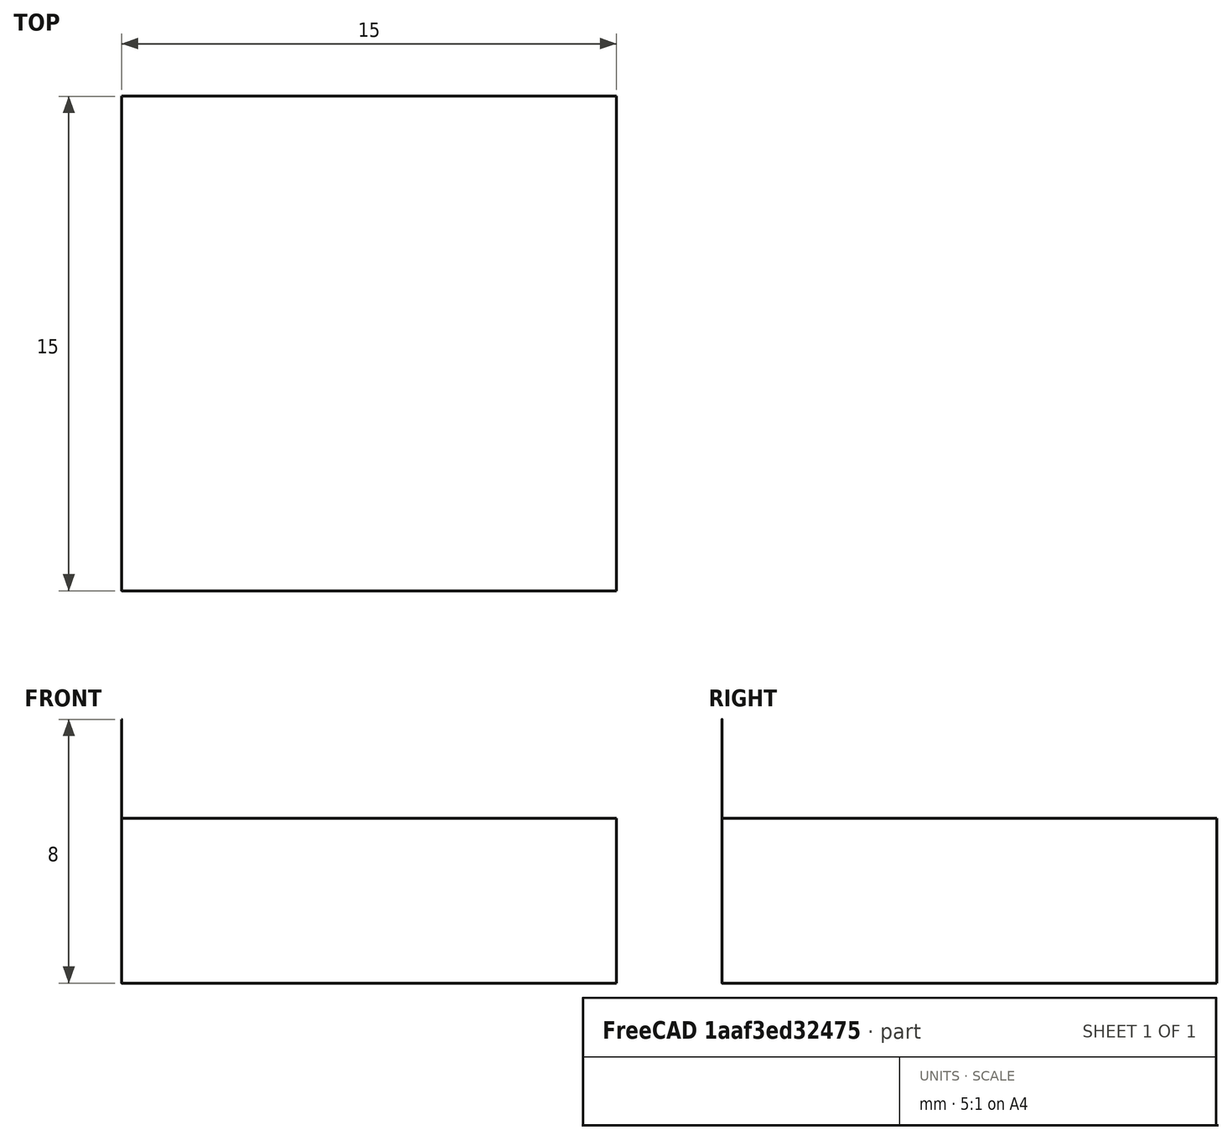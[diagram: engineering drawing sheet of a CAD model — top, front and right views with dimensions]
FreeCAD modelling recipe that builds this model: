
FCSTD DOCUMENT  (FreeCAD 1.0R39109 (Git))
Label: BoxWith36GridPockets
License: All rights reserved
LicenseURL: https://en.wikipedia.org/wiki/All_rights_reserved
objects: Part::Box×37, Part::Cut×36, Part::FeaturePython×3, App::DocumentObjectGroup×3, Path::FeaturePython×3, App::FeaturePython×1
note: 77 computed .brp shape members not serialized (recipe doc carries the construction recipe); baked Part::Feature solids carry a one-line shape summary decoded from their .brp

FEATURE [Part::Box] Box
  AttacherType = Attacher::AttachEngine3D
  Height = 5
  Length = 15
  Width = 15
FEATURE [Part::Box] Pocket_0_0
  AttacherType = Attacher::AttachEngine3D
  Height = 0.01
  Length = 0.2
  Placement = pos=(1.97143,1.97143,4.99) rot=(0,0,1;0rad)
  Width = 0.2
FEATURE [Part::Box] Pocket_0_1
  AttacherType = Attacher::AttachEngine3D
  Height = 0.01
  Length = 0.2
  Placement = pos=(4.14286,1.97143,4.99) rot=(0,0,1;0rad)
  Width = 0.2
FEATURE [Part::Box] Pocket_0_2
  AttacherType = Attacher::AttachEngine3D
  Height = 0.01
  Length = 0.2
  Placement = pos=(6.31429,1.97143,4.99) rot=(0,0,1;0rad)
  Width = 0.2
FEATURE [Part::Box] Pocket_0_3
  AttacherType = Attacher::AttachEngine3D
  Height = 0.01
  Length = 0.2
  Placement = pos=(8.48571,1.97143,4.99) rot=(0,0,1;0rad)
  Width = 0.2
FEATURE [Part::Box] Pocket_0_4
  AttacherType = Attacher::AttachEngine3D
  Height = 0.01
  Length = 0.2
  Placement = pos=(10.6571,1.97143,4.99) rot=(0,0,1;0rad)
  Width = 0.2
FEATURE [Part::Box] Pocket_0_5
  AttacherType = Attacher::AttachEngine3D
  Height = 0.01
  Length = 0.2
  Placement = pos=(12.8286,1.97143,4.99) rot=(0,0,1;0rad)
  Width = 0.2
FEATURE [Part::Box] Pocket_1_0
  AttacherType = Attacher::AttachEngine3D
  Height = 0.01
  Length = 0.2
  Placement = pos=(1.97143,4.14286,4.99) rot=(0,0,1;0rad)
  Width = 0.2
FEATURE [Part::Box] Pocket_1_1
  AttacherType = Attacher::AttachEngine3D
  Height = 0.01
  Length = 0.2
  Placement = pos=(4.14286,4.14286,4.99) rot=(0,0,1;0rad)
  Width = 0.2
FEATURE [Part::Box] Pocket_1_2
  AttacherType = Attacher::AttachEngine3D
  Height = 0.01
  Length = 0.2
  Placement = pos=(6.31429,4.14286,4.99) rot=(0,0,1;0rad)
  Width = 0.2
FEATURE [Part::Box] Pocket_1_3
  AttacherType = Attacher::AttachEngine3D
  Height = 0.01
  Length = 0.2
  Placement = pos=(8.48571,4.14286,4.99) rot=(0,0,1;0rad)
  Width = 0.2
FEATURE [Part::Box] Pocket_1_4
  AttacherType = Attacher::AttachEngine3D
  Height = 0.01
  Length = 0.2
  Placement = pos=(10.6571,4.14286,4.99) rot=(0,0,1;0rad)
  Width = 0.2
FEATURE [Part::Box] Pocket_1_5
  AttacherType = Attacher::AttachEngine3D
  Height = 0.01
  Length = 0.2
  Placement = pos=(12.8286,4.14286,4.99) rot=(0,0,1;0rad)
  Width = 0.2
FEATURE [Part::Box] Pocket_2_0
  AttacherType = Attacher::AttachEngine3D
  Height = 0.01
  Length = 0.2
  Placement = pos=(1.97143,6.31429,4.99) rot=(0,0,1;0rad)
  Width = 0.2
FEATURE [Part::Box] Pocket_2_1
  AttacherType = Attacher::AttachEngine3D
  Height = 0.01
  Length = 0.2
  Placement = pos=(4.14286,6.31429,4.99) rot=(0,0,1;0rad)
  Width = 0.2
FEATURE [Part::Box] Pocket_2_2
  AttacherType = Attacher::AttachEngine3D
  Height = 0.01
  Length = 0.2
  Placement = pos=(6.31429,6.31429,4.99) rot=(0,0,1;0rad)
  Width = 0.2
FEATURE [Part::Box] Pocket_2_3
  AttacherType = Attacher::AttachEngine3D
  Height = 0.01
  Length = 0.2
  Placement = pos=(8.48571,6.31429,4.99) rot=(0,0,1;0rad)
  Width = 0.2
FEATURE [Part::Box] Pocket_2_4
  AttacherType = Attacher::AttachEngine3D
  Height = 0.01
  Length = 0.2
  Placement = pos=(10.6571,6.31429,4.99) rot=(0,0,1;0rad)
  Width = 0.2
FEATURE [Part::Box] Pocket_2_5
  AttacherType = Attacher::AttachEngine3D
  Height = 0.01
  Length = 0.2
  Placement = pos=(12.8286,6.31429,4.99) rot=(0,0,1;0rad)
  Width = 0.2
FEATURE [Part::Box] Pocket_3_0
  AttacherType = Attacher::AttachEngine3D
  Height = 0.01
  Length = 0.2
  Placement = pos=(1.97143,8.48571,4.99) rot=(0,0,1;0rad)
  Width = 0.2
FEATURE [Part::Box] Pocket_3_1
  AttacherType = Attacher::AttachEngine3D
  Height = 0.01
  Length = 0.2
  Placement = pos=(4.14286,8.48571,4.99) rot=(0,0,1;0rad)
  Width = 0.2
FEATURE [Part::Box] Pocket_3_2
  AttacherType = Attacher::AttachEngine3D
  Height = 0.01
  Length = 0.2
  Placement = pos=(6.31429,8.48571,4.99) rot=(0,0,1;0rad)
  Width = 0.2
FEATURE [Part::Box] Pocket_3_3
  AttacherType = Attacher::AttachEngine3D
  Height = 0.01
  Length = 0.2
  Placement = pos=(8.48571,8.48571,4.99) rot=(0,0,1;0rad)
  Width = 0.2
FEATURE [Part::Box] Pocket_3_4
  AttacherType = Attacher::AttachEngine3D
  Height = 0.01
  Length = 0.2
  Placement = pos=(10.6571,8.48571,4.99) rot=(0,0,1;0rad)
  Width = 0.2
FEATURE [Part::Box] Pocket_3_5
  AttacherType = Attacher::AttachEngine3D
  Height = 0.01
  Length = 0.2
  Placement = pos=(12.8286,8.48571,4.99) rot=(0,0,1;0rad)
  Width = 0.2
FEATURE [Part::Box] Pocket_4_0
  AttacherType = Attacher::AttachEngine3D
  Height = 0.01
  Length = 0.2
  Placement = pos=(1.97143,10.6571,4.99) rot=(0,0,1;0rad)
  Width = 0.2
FEATURE [Part::Box] Pocket_4_1
  AttacherType = Attacher::AttachEngine3D
  Height = 0.01
  Length = 0.2
  Placement = pos=(4.14286,10.6571,4.99) rot=(0,0,1;0rad)
  Width = 0.2
FEATURE [Part::Box] Pocket_4_2
  AttacherType = Attacher::AttachEngine3D
  Height = 0.01
  Length = 0.2
  Placement = pos=(6.31429,10.6571,4.99) rot=(0,0,1;0rad)
  Width = 0.2
FEATURE [Part::Box] Pocket_4_3
  AttacherType = Attacher::AttachEngine3D
  Height = 0.01
  Length = 0.2
  Placement = pos=(8.48571,10.6571,4.99) rot=(0,0,1;0rad)
  Width = 0.2
FEATURE [Part::Box] Pocket_4_4
  AttacherType = Attacher::AttachEngine3D
  Height = 0.01
  Length = 0.2
  Placement = pos=(10.6571,10.6571,4.99) rot=(0,0,1;0rad)
  Width = 0.2
FEATURE [Part::Box] Pocket_4_5
  AttacherType = Attacher::AttachEngine3D
  Height = 0.01
  Length = 0.2
  Placement = pos=(12.8286,10.6571,4.99) rot=(0,0,1;0rad)
  Width = 0.2
FEATURE [Part::Box] Pocket_5_0
  AttacherType = Attacher::AttachEngine3D
  Height = 0.01
  Length = 0.2
  Placement = pos=(1.97143,12.8286,4.99) rot=(0,0,1;0rad)
  Width = 0.2
FEATURE [Part::Box] Pocket_5_1
  AttacherType = Attacher::AttachEngine3D
  Height = 0.01
  Length = 0.2
  Placement = pos=(4.14286,12.8286,4.99) rot=(0,0,1;0rad)
  Width = 0.2
FEATURE [Part::Box] Pocket_5_2
  AttacherType = Attacher::AttachEngine3D
  Height = 0.01
  Length = 0.2
  Placement = pos=(6.31429,12.8286,4.99) rot=(0,0,1;0rad)
  Width = 0.2
FEATURE [Part::Box] Pocket_5_3
  AttacherType = Attacher::AttachEngine3D
  Height = 0.01
  Length = 0.2
  Placement = pos=(8.48571,12.8286,4.99) rot=(0,0,1;0rad)
  Width = 0.2
FEATURE [Part::Box] Pocket_5_4
  AttacherType = Attacher::AttachEngine3D
  Height = 0.01
  Length = 0.2
  Placement = pos=(10.6571,12.8286,4.99) rot=(0,0,1;0rad)
  Width = 0.2
FEATURE [Part::Box] Pocket_5_5
  AttacherType = Attacher::AttachEngine3D
  Height = 0.01
  Length = 0.2
  Placement = pos=(12.8286,12.8286,4.99) rot=(0,0,1;0rad)
  Width = 0.2
FEATURE [Part::Cut] Cut  label="Cut_0"
  Base = -> Box
  Refine = true
  Tool = -> Pocket_0_0
FEATURE [Part::Cut] Cut001  label="Cut_1"
  Base = -> Cut
  Refine = true
  Tool = -> Pocket_0_1
FEATURE [Part::Cut] Cut002  label="Cut_2"
  Base = -> Cut001
  Refine = true
  Tool = -> Pocket_0_2
FEATURE [Part::Cut] Cut003  label="Cut_3"
  Base = -> Cut002
  Refine = true
  Tool = -> Pocket_0_3
FEATURE [Part::Cut] Cut004  label="Cut_4"
  Base = -> Cut003
  Refine = true
  Tool = -> Pocket_0_4
FEATURE [Part::Cut] Cut005  label="Cut_5"
  Base = -> Cut004
  Refine = true
  Tool = -> Pocket_0_5
FEATURE [Part::Cut] Cut006  label="Cut_6"
  Base = -> Cut005
  Refine = true
  Tool = -> Pocket_1_0
FEATURE [Part::Cut] Cut007  label="Cut_7"
  Base = -> Cut006
  Refine = true
  Tool = -> Pocket_1_1
FEATURE [Part::Cut] Cut008  label="Cut_8"
  Base = -> Cut007
  Refine = true
  Tool = -> Pocket_1_2
FEATURE [Part::Cut] Cut009  label="Cut_9"
  Base = -> Cut008
  Refine = true
  Tool = -> Pocket_1_3
FEATURE [Part::Cut] Cut010  label="Cut_10"
  Base = -> Cut009
  Refine = true
  Tool = -> Pocket_1_4
FEATURE [Part::Cut] Cut011  label="Cut_11"
  Base = -> Cut010
  Refine = true
  Tool = -> Pocket_1_5
FEATURE [Part::Cut] Cut012  label="Cut_12"
  Base = -> Cut011
  Refine = true
  Tool = -> Pocket_2_0
FEATURE [Part::Cut] Cut013  label="Cut_13"
  Base = -> Cut012
  Refine = true
  Tool = -> Pocket_2_1
FEATURE [Part::Cut] Cut014  label="Cut_14"
  Base = -> Cut013
  Refine = true
  Tool = -> Pocket_2_2
FEATURE [Part::Cut] Cut015  label="Cut_15"
  Base = -> Cut014
  Refine = true
  Tool = -> Pocket_2_3
FEATURE [Part::Cut] Cut016  label="Cut_16"
  Base = -> Cut015
  Refine = true
  Tool = -> Pocket_2_4
FEATURE [Part::Cut] Cut017  label="Cut_17"
  Base = -> Cut016
  Refine = true
  Tool = -> Pocket_2_5
FEATURE [Part::Cut] Cut018  label="Cut_18"
  Base = -> Cut017
  Refine = true
  Tool = -> Pocket_3_0
FEATURE [Part::Cut] Cut019  label="Cut_19"
  Base = -> Cut018
  Refine = true
  Tool = -> Pocket_3_1
FEATURE [Part::Cut] Cut020  label="Cut_20"
  Base = -> Cut019
  Refine = true
  Tool = -> Pocket_3_2
FEATURE [Part::Cut] Cut021  label="Cut_21"
  Base = -> Cut020
  Refine = true
  Tool = -> Pocket_3_3
FEATURE [Part::Cut] Cut022  label="Cut_22"
  Base = -> Cut021
  Refine = true
  Tool = -> Pocket_3_4
FEATURE [Part::Cut] Cut023  label="Cut_23"
  Base = -> Cut022
  Refine = true
  Tool = -> Pocket_3_5
FEATURE [Part::Cut] Cut024  label="Cut_24"
  Base = -> Cut023
  Refine = true
  Tool = -> Pocket_4_0
FEATURE [Part::Cut] Cut025  label="Cut_25"
  Base = -> Cut024
  Refine = true
  Tool = -> Pocket_4_1
FEATURE [Part::Cut] Cut026  label="Cut_26"
  Base = -> Cut025
  Refine = true
  Tool = -> Pocket_4_2
FEATURE [Part::Cut] Cut027  label="Cut_27"
  Base = -> Cut026
  Refine = true
  Tool = -> Pocket_4_3
FEATURE [Part::Cut] Cut028  label="Cut_28"
  Base = -> Cut027
  Refine = true
  Tool = -> Pocket_4_4
FEATURE [Part::Cut] Cut029  label="Cut_29"
  Base = -> Cut028
  Refine = true
  Tool = -> Pocket_4_5
FEATURE [Part::Cut] Cut030  label="Cut_30"
  Base = -> Cut029
  Refine = true
  Tool = -> Pocket_5_0
FEATURE [Part::Cut] Cut031  label="Cut_31"
  Base = -> Cut030
  Refine = true
  Tool = -> Pocket_5_1
FEATURE [Part::Cut] Cut032  label="Cut_32"
  Base = -> Cut031
  Refine = true
  Tool = -> Pocket_5_2
FEATURE [Part::Cut] Cut033  label="Cut_33"
  Base = -> Cut032
  Refine = true
  Tool = -> Pocket_5_3
FEATURE [Part::Cut] Cut034  label="Cut_34"
  Base = -> Cut033
  Refine = true
  Tool = -> Pocket_5_4
FEATURE [Part::Cut] Cut035  label="Cut_35"
  Base = -> Cut034
  Refine = true
  Tool = -> Pocket_5_5
FEATURE [App::FeaturePython] SetupSheet  # Path/CAM operation (typed FeaturePython)
  ClearanceHeightExpression = OpStockZMax+SetupSheet.ClearanceHeightOffset
  ClearanceHeightOffset = 5
  CoolantMode = 0
  CoolantModes = None | Flood | Mist
  FinalDepthExpression = OpFinalDepth
  HorizRapid = 0
  SafeHeightExpression = OpStockZMax+SetupSheet.SafeHeightOffset
  SafeHeightOffset = 3
  StartDepthExpression = OpStartDepth
  StepDownExpression = OpToolDiameter
  VertRapid = 0
FEATURE [Part::FeaturePython] Clone  label="Model-Cut_35"  # Draft clone (typed FeaturePython)
  AttacherType = Attacher::AttachEngine3D
  Fuse = false
  Objects = -> [Cut035]
  PathResource = Model
  Scale = (1,1,1)
FEATURE [App::DocumentObjectGroup] Model
  Group = -> [Clone]
FEATURE [Part::FeaturePython] ToolBit  label="Drill"  # Path/CAM toolbit (typed FeaturePython)
  BitPropertyNames = Chipload | Diameter | Flutes | Length | Material | TipAngle
  BitShape = <path>
  Chipload = 0
  Diameter = 0.005
  Flutes = 0
  Length = 8
  Material = 0
  ShapeName = drill
  TipAngle = 119
FEATURE [Path::FeaturePython] TC__Default_Tool  label="TC: Default Tool"  # Path/CAM operation (typed FeaturePython)
  HorizFeed = 0
  HorizRapid = 0
  SpindleDir = 0
  SpindleSpeed = 0
  Tool = -> ToolBit
  ToolNumber = 1
  VertFeed = 0
  VertRapid = 0
  expr: HorizRapid = SetupSheet.HorizRapid
  expr: VertRapid = SetupSheet.VertRapid
FEATURE [App::DocumentObjectGroup] Tools
  Group = -> [TC__Default_Tool]
FEATURE [Part::FeaturePython] Stock  # WARN: FeaturePython — macro-defined, semantics opaque (R4)
  Base = -> Model
  ExtXneg = 0.001
  ExtXpos = 0.001
  ExtYneg = 0.001
  ExtYpos = 0.001
  ExtZneg = 0.001
  ExtZpos = 0.001
  StockType = FromBase
FEATURE [Path::FeaturePython] Pocket_Shape  # Path/CAM operation (typed FeaturePython)
  Active = true
  AreaParams:
    Tolerance = 1e-07
    FitArcs = True
    Simplify = False
    CleanDistance = 0.0
    Accuracy = 0.01
    Unit = 1.0
    MinArcPoints = 4
    MaxArcPoints = 100
    ClipperScale = 10000000.0
    Fill = 0
    Coplanar = 0
    Reorient = True
    Outline = False
    Explode = False
    OpenMode = 0
    Deflection = 0.01
    SubjectFill = 0
    ClipFill = 0
    Offset = 0.0
    ExtraPass = 0
    Stepover = 0.0
    LastStepover = 0.0
    JoinType = 0
    EndType = 0
    MiterLimit = 2.0
    RoundPrecision = 0.0
    PocketMode = 1
    ToolRadius = 0.0025
    PocketExtraOffset = 0.0
    PocketStepover = 0.0025
    PocketLastStepover = 0.0
    FromCenter = True
    Angle = 0.0
    AngleShift = 0.0
    Shift = 0.0
    Thicken = False
    SectionCount = -1
    Stepdown = 1.0
    SectionOffset = 0.0
    SectionTolerance = 1e-06
    SectionMode = 2
    Project = False
  Base = -> [Clone]
  ClearanceHeight = 10.001
  CoolantMode = 0
  CutMode = 0
  CycleTime = Cycletime Error
  ExtensionCorners = true
  ExtensionLengthDefault = 0.0025
  ExtraOffset = 0
  FinalDepth = 4.99
  FinishDepth = 0
  KeepToolDown = false
  MinTravel = false
  OffsetPattern = 0
  OpFinalDepth = 4.99
  OpStartDepth = 5.001
  OpStockZMax = 5.001
  OpStockZMin = -0.001
  OpToolDiameter = 0.005
  PathParams = {'orientation': 1, 'feedrate': 0.0, 'feedrate_v': 0.0, 'verbose': True, 'resume_height': 8.001000000000001, 'retraction': 10.001000000000001, 'return_end': True, 'preamble': False, 'start': Vector (12.831071528571428, 4.145357142857144, 10.001000000000001)}
  PocketLastStepOver = 0
  SafeHeight = 8.001
  SplitArcs = false
  StartAt = 0
  StartDepth = 5.001
  StartPoint = (0,0,0)
  StepDown = 0.005
  StepOver = 50
  ToolController = -> TC__Default_Tool
  UseOutline = false
  UseRestMachining = false
  UseStartPoint = false
  ZigZagAngle = 0
  expr: ClearanceHeight = OpStockZMax + SetupSheet.ClearanceHeightOffset
  expr: ExtensionLengthDefault = OpToolDiameter / 2
  expr: FinalDepth = OpFinalDepth
  expr: SafeHeight = OpStockZMax + SetupSheet.SafeHeightOffset
  expr: StartDepth = OpStartDepth
  expr: StepDown = OpToolDiameter
FEATURE [App::DocumentObjectGroup] Operations
  Group = -> [Pocket_Shape]
FEATURE [Path::FeaturePython] Job  # Path/CAM operation (typed FeaturePython)
  CycleTime = 00:00:00
  Fixtures = G54
  GeometryTolerance = 0.01
  JobType = 0
  Model = -> Model
  Operations = -> Operations
  OrderOutputBy = 0
  PostProcessor = 14
  PostProcessorOutputFile = <userpath>/Desktop/freecad/laser36pockets_10layers.mpf
  SetupSheet = -> SetupSheet
  SplitOutput = false
  Stock = -> Stock
  Tools = -> Tools
note: 1 file-system path scrubbed to <path> (originals preserved in the JSON sidecar)
